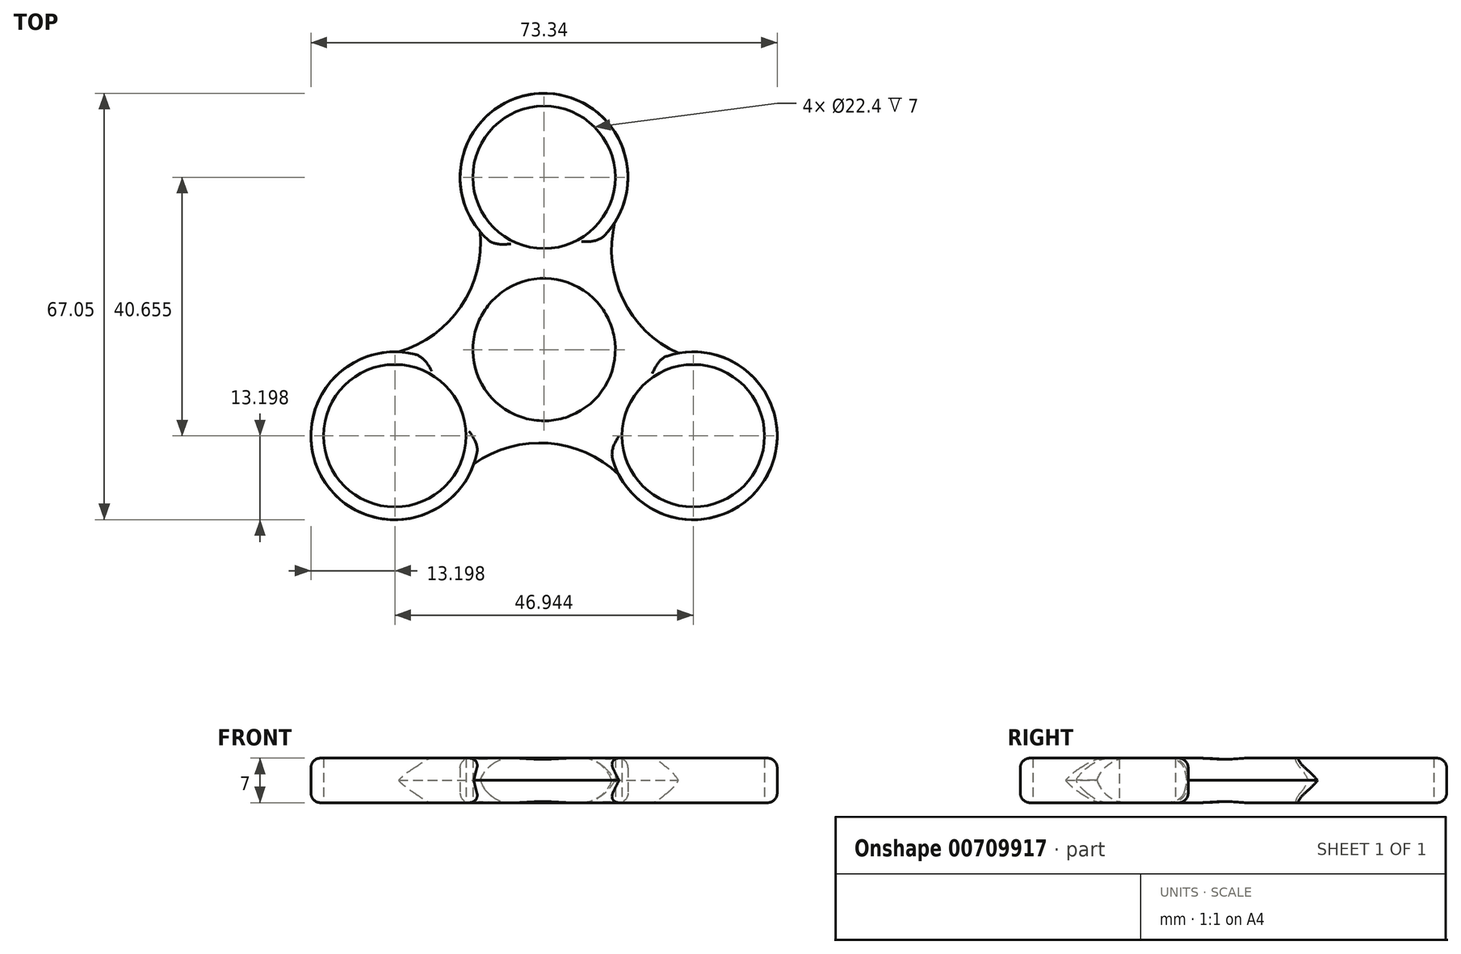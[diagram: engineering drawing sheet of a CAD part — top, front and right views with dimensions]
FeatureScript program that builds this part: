
annotation { "Feature Type Name" : "Feature", "Feature Type Description" : "" }
export const myFeature = defineFeature(function(context is Context, id is Id, definition is map)
    precondition{}
    {
        {
            var Q0;
            Q0=qCreatedBy(makeId("Top.planeOp"),FACE);
            var sketch = newSketch(context, id + "F0", { "sketchPlane" : qUnion([Q0])});
            skCircle(sketch, "E0", {"center": v(0, 0) * mm, "radius": 11.2 * mm});
            skCircle(sketch, "E1", {"center": v(0, 27.1) * mm, "radius": 11.2 * mm});
            skArc(sketch, "E2", {"start": v(11.56, 20.74) * mm, "mid": v(-1.11, 40.26) * mm, "end": v(-10.33, 18.88) * mm});
            skArc(sketch, "E3.1.0", {"start": v(-23.74, -0.35) * mm, "mid": v(-34.3, -21.1) * mm, "end": v(-11.19, -18.39) * mm});
            skCircle(sketch, "E3.1.1", {"center": v(-23.47, -13.55) * mm, "radius": 11.2 * mm});
            skArc(sketch, "E3.2.0", {"start": v(12.18, -20.38) * mm, "mid": v(35.42, -19.16) * mm, "end": v(21.52, -0.5) * mm});
            skCircle(sketch, "E3.2.1", {"center": v(23.47, -13.55) * mm, "radius": 11.2 * mm});
            skArc(sketch, "E4", {"start": v(11.56, 20.74) * mm, "mid": v(12.53, 8.24) * mm, "end": v(21.52, -0.5) * mm});
            skArc(sketch, "E5.1.0", {"start": v(-23.74, -0.35) * mm, "mid": v(-13.4, 6.73) * mm, "end": v(-10.33, 18.88) * mm});
            skArc(sketch, "E5.2.0", {"start": v(12.18, -20.38) * mm, "mid": v(0.87, -14.97) * mm, "end": v(-11.19, -18.39) * mm});
            skSolve(sketch);
        }
        {
            var Q0;
            Q0=makeQuery(id+"F0.imprint","IMPRINT",FACE,{"disambiguationData":[TD([[makeQuery(id+"F0.imprint","IMPRINT",EDGE,{"derivedFrom":sQuery(id+"F0.wireOp",EDGE,"E0")}),-1.0]])]});
            extrude(context, id + "F1", {"entities" : qUnion([Q0]), "depth" : 7 * mm, "offsetDistance" : 25 * mm});
        }
        {
            var Q0;
            Q0=makeQuery(id+"F1.opExtrude","CAP_EDGE",EDGE,{"disambiguationData":[OSD([sQuery(id+"F0.wireOp",EDGE,"E5.2.0")])],"isStart":false});
            var Q1;
            Q1=makeQuery(id+"F1.opExtrude","CAP_EDGE",EDGE,{"disambiguationData":[OSD([sQuery(id+"F0.wireOp",EDGE,"E4")])],"isStart":false});
            var Q2;
            Q2=makeQuery(id+"F1.opExtrude","CAP_EDGE",EDGE,{"disambiguationData":[OSD([sQuery(id+"F0.wireOp",EDGE,"E5.1.0")])],"isStart":false});
            var Q3;
            Q3=makeQuery(id+"F1.opExtrude","CAP_EDGE",EDGE,{"disambiguationData":[OSD([sQuery(id+"F0.wireOp",EDGE,"E5.2.0")])],"isStart":true});
            var Q4;
            Q4=makeQuery(id+"F1.opExtrude","CAP_EDGE",EDGE,{"disambiguationData":[OSD([sQuery(id+"F0.wireOp",EDGE,"E5.1.0")])],"isStart":true});
            var Q5;
            Q5=makeQuery(id+"F1.opExtrude","CAP_EDGE",EDGE,{"disambiguationData":[OSD([sQuery(id+"F0.wireOp",EDGE,"E4")])],"isStart":true});
            fillet(context, id + "F2", {"entities" : qUnion([Q0, Q1, Q2, Q3, Q4, Q5]), "radius" : 5 * mm, "tangentPropagation" : true, "allowEdgeOverflow" : false});
        }
        {
            var Q0;
            Q0=makeQuery(id+"F1.opExtrude","CAP_EDGE",EDGE,{"disambiguationData":[OSD([sQuery(id+"F0.wireOp",EDGE,"E3.1.0")])],"isStart":false});
            var Q1;
            Q1=makeQuery(id+"F1.opExtrude","CAP_EDGE",EDGE,{"disambiguationData":[OSD([sQuery(id+"F0.wireOp",EDGE,"E2")])],"isStart":false});
            var Q2;
            Q2=makeQuery(id+"F1.opExtrude","CAP_EDGE",EDGE,{"disambiguationData":[OSD([sQuery(id+"F0.wireOp",EDGE,"E3.2.0")])],"isStart":false});
            var Q3;
            Q3=makeQuery(id+"F1.opExtrude","CAP_EDGE",EDGE,{"disambiguationData":[OSD([sQuery(id+"F0.wireOp",EDGE,"E3.2.0")])],"isStart":true});
            var Q4;
            Q4=makeQuery(id+"F1.opExtrude","CAP_EDGE",EDGE,{"disambiguationData":[OSD([sQuery(id+"F0.wireOp",EDGE,"E2")])],"isStart":true});
            var Q5;
            Q5=makeQuery(id+"F1.opExtrude","CAP_EDGE",EDGE,{"disambiguationData":[OSD([sQuery(id+"F0.wireOp",EDGE,"E3.1.0")])],"isStart":true});
            fillet(context, id + "F3", {"entities" : qUnion([Q0, Q1, Q2, Q3, Q4, Q5]), "radius" : 1.5 * mm, "tangentPropagation" : true, "allowEdgeOverflow" : false});
        }
    });
